# Revit family: 6700 Piloti Table
name_source: partatom
category: Furniture
revit_build: Autodesk Revit 2017 (Build: 20171027_0315(x64)
units: mm (PartAtom-declared; Revit-internal decimal feet)

## family parameters
Always vertical = Yes
Cut with Voids When Loaded = No
OmniClass Number = 23.40.20.00
OmniClass Title = General Furniture and Specialties
Room Calculation Point = No
Shared = No
Work Plane-Based = No

## types (2) — shared parameters
Description = Piloti is a series of solid oak side tables. The subtle detailing of the table top creates the impression of a single line, floating between four delicate legs. The tables are supplied in two heights and can be combined as a nest.
Design year = 2016
Designer = Hugo Passos
Item No. = 6700
Legs = FF Black Lacquered vertical
Length = 390 mm  [stored 1.27953 ft]
Manufacturer = Fredericia Furniture
Model = Piloti Table
Table Top = FF Black Lacquered horizontal
Tabletop = Piloti TableTop 6700
URL = https://www.fredericia.com
Variations Tabletop and frame by request = Available in Oak lacquered and white oil
Variations Tabletop and frame standard = Available in oak soap, oak oiled, oak black lacquered and smoked oak oiled
Weight = 2,3 kg
Width = 310 mm  [stored 1.01706 ft]

## per-type parameters (varying)
| type | Height | Leg Height |
| 6700 Piloti Table L39xW31 H35 | 350 mm  [stored 1.14829 ft] | 324 mm  [stored 1.06299 ft] |
| 6700 Piloti Table L39xW31 H41 | 410 mm  [stored 1.34514 ft] | 384 mm  [stored 1.25984 ft] |

note: [stored X ft] marks values corroborated as IEEE doubles in the binary element streams (Revit-internal decimal feet)

## geometry (parser evidence)
native form markers: Sweep x8
no freeform markers — native parametric forms only
